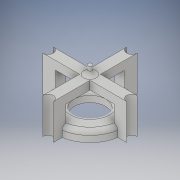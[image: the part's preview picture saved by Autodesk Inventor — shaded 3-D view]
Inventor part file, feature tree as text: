
AUTODESK INVENTOR PART (.ipt)
format: ipt  version: 2019 (Build 230136000, 136)  size: 245,760 bytes
history: native  units: mm
features: extrude x5, sketch x5, fillet x2
ambient origin geometry x8: Origin, YZ Plane, XZ Plane, XY Plane, X Axis, Y Axis, Z Axis, Center Point
bodies: Body1 (feature_tree)
feature tree (12):
  extrude  "Extrusion15"  Depth=32.0mm
  extrude  "Extrusion16"  Depth=2.5mm
  extrude  "Extrusion17"  Depth=2.5mm
  extrude  "Extrusion18"  Depth=5.0mm TaperAngle=0.0deg
  extrude  "Extrusion19"  Depth=2.0mm
  fillet  "Fillet1"  Radius=1.0mm
  fillet  "Fillet2"  Radius=8.0mm
  sketch  "Sketch14"  dims[d4=30.0mm d48=32.0mm d86=32.0mm]
  sketch  "Sketch15"  dims[d87=2.5mm d88=2.5mm]
  sketch  "Sketch16"  dims[d89=2.5mm d90=2.5mm]
  sketch  "Sketch17"  dims[d91=15.0mm d92=5.0mm d93=0.0mm]
  sketch  "Sketch18"  dims[d94=17.0mm d95=30.0mm d96=1.0mm d97=0.0mm d98=8.0mm d99=0.0mm d100=4.0mm d101=0.0mm d102=2.0mm d103=4.0mm d104=0.0mm d105=2.0mm d106=2.0mm]
